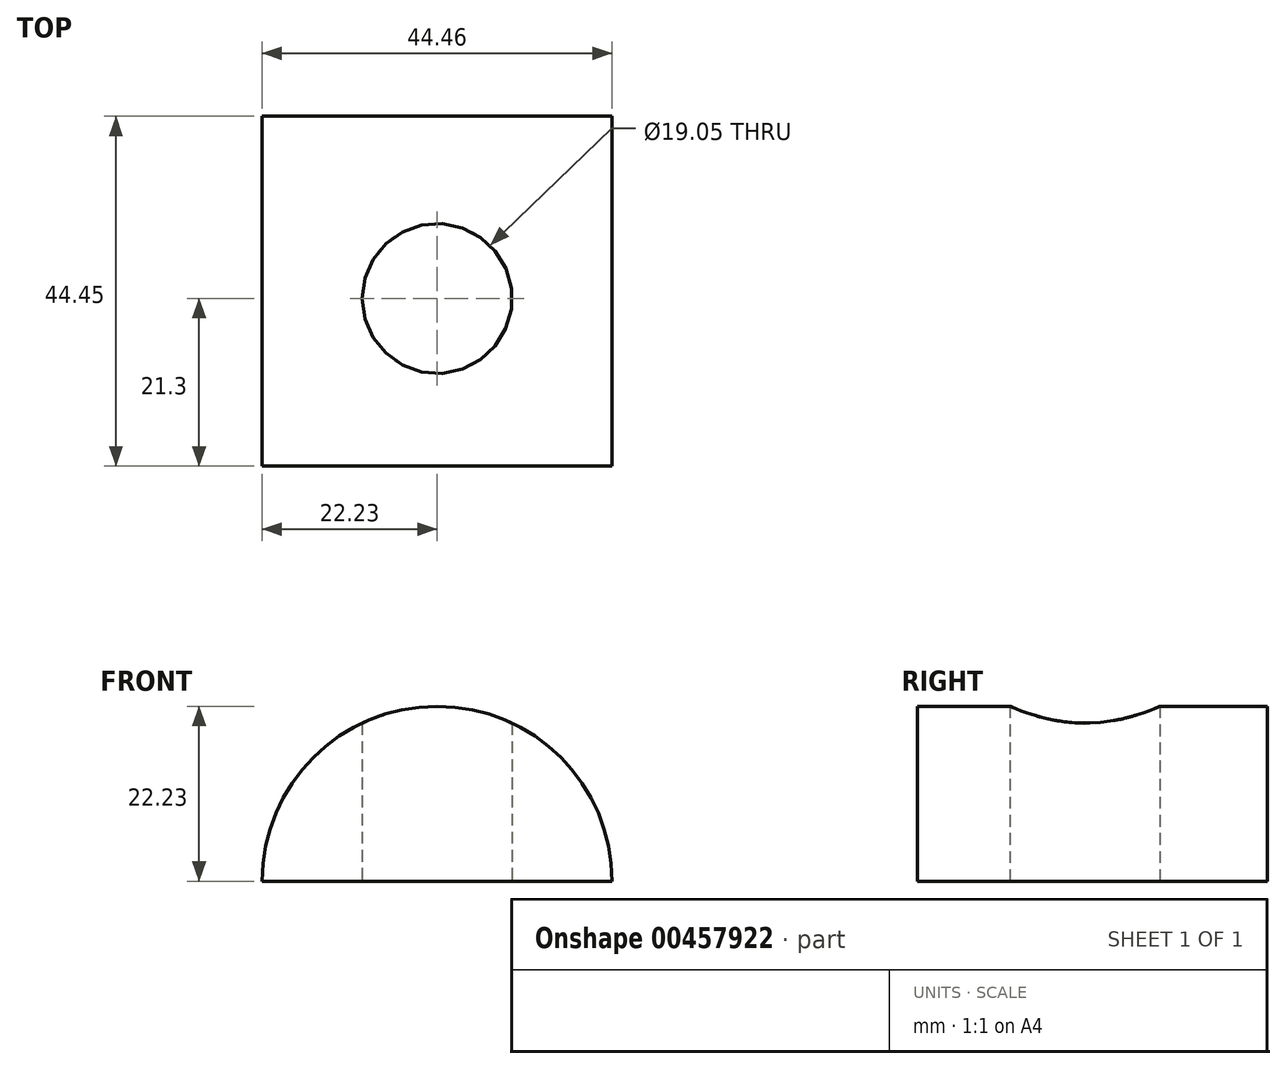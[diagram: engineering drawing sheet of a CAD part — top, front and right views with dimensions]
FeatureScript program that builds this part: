
annotation { "Feature Type Name" : "Feature", "Feature Type Description" : "" }
export const myFeature = defineFeature(function(context is Context, id is Id, definition is map)
    precondition{}
    {
        {
            var Q0;
            Q0=qCreatedBy(makeId("Front.planeOp"),FACE);
            var sketch = newSketch(context, id + "F0", { "sketchPlane" : qUnion([Q0])});
            skArc(sketch, "E0", {"start": v(-22.23, 0) * mm, "mid": v(0, 22.23) * mm, "end": v(22.23, 0) * mm});
            skLineSegment(sketch, "E1", {"start": v(-22.23, 0) * mm, "end": v(22.23, 0) * mm});
            skSolve(sketch);
        }
        {
            var Q0;
            Q0 = qSketchRegion(id + "F0", true);
            extrude(context, id + "F1", {"entities" : qUnion([Q0]), "depth" : 44.45 * mm});
        }
        {
            var Q0;
            Q0=qCreatedBy(makeId("Top.planeOp"),FACE);
            var sketch = newSketch(context, id + "F2", { "sketchPlane" : qUnion([Q0])});
            skCircle(sketch, "E2", {"center": v(0, -23.15) * mm, "radius": 9.53 * mm});
            skSolve(sketch);
        }
        {
            var Q0;
            Q0 = qSketchRegion(id + "F2", true);
            extrude(context, id + "F3", {"entities" : qUnion([Q0]), "operationType" : NewBodyOperationType.REMOVE, "endBound" : BoundingType.THROUGH_ALL, "depth" : 25.4 * mm});
        }
    });
